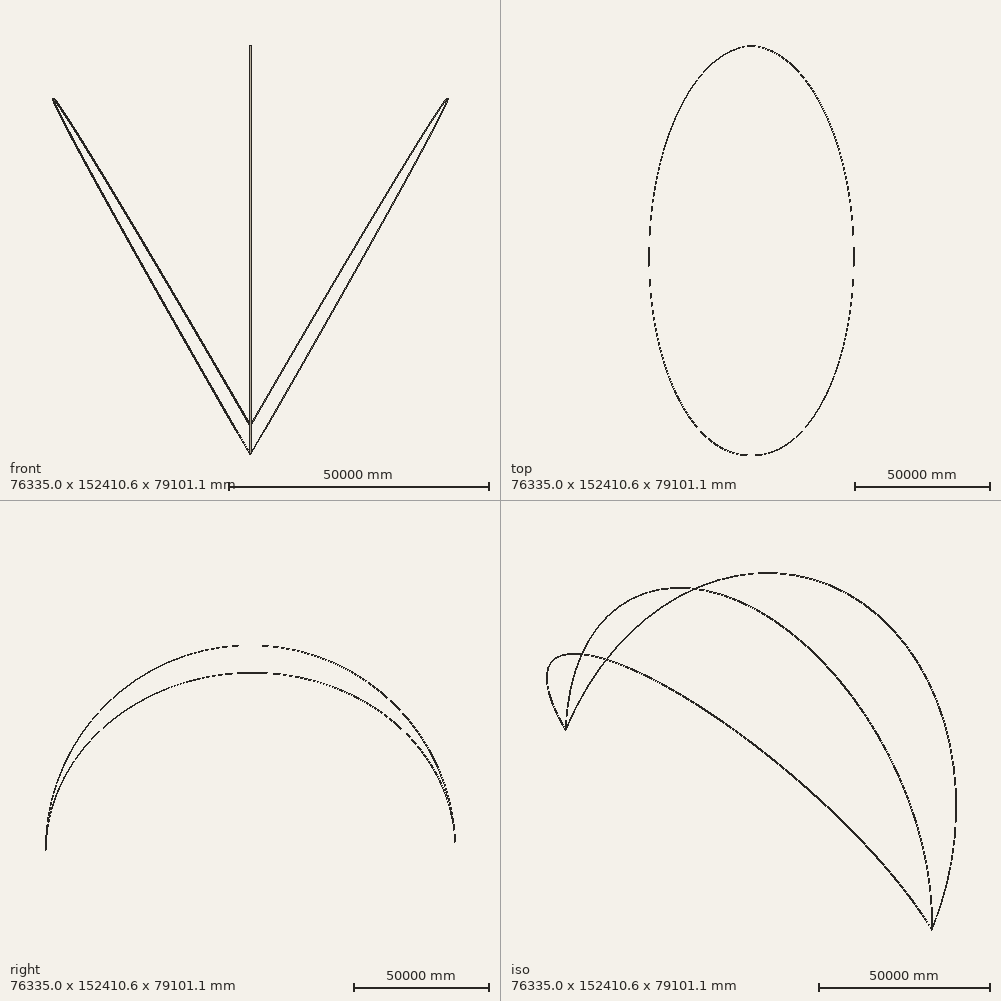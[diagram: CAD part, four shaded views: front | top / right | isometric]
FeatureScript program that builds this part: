
annotation { "Feature Type Name" : "Feature", "Feature Type Description" : "" }
export const myFeature = defineFeature(function(context is Context, id is Id, definition is map)
    precondition{}
    {
        {
            var Q0;
            Q0=qCreatedBy(makeId("Right.planeOp"),FACE);
            var sketch = newSketch(context, id + "F0", { "sketchPlane" : qUnion([Q0])});
            skArc(sketch, "E0", {"start": v(76147.78, 2820.45) * mm, "mid": v(-2820.45, 76147.78) * mm, "end": v(-76147.78, -2820.45) * mm});
            skLineSegment(sketch, "E1", {"start": v(76147.78, 2820.45) * mm, "end": v(-76147.78, -2820.45) * mm});
            skSolve(sketch);
        }
        {
            var Q0;
            Q0=makeQuery(id+"F0.imprint","IMPRINT",FACE,{"disambiguationData":[TD([[makeQuery(id+"F0.imprint","IMPRINT",EDGE,{"derivedFrom":sQuery(id+"F0.wireOp",EDGE,"E0")}),1.0]])]});
            var Q1;
            Q1=sQuery(id+"F0.wireOp",EDGE,"E1");
            cPlane(context, id + "F1", {"entities" : qUnion([Q0, Q1]), "cplaneType" : CPlaneType.LINE_ANGLE, "offset" : 25.4 * mm, "angle" : 30 * degree, "width" : 152.4 * mm, "height" : 152.4 * mm});
        }
        {
            var Q0;
            Q0=qCreatedBy(makeId("Top.planeOp"),FACE);
            var sketch = newSketch(context, id + "F2", { "sketchPlane" : qUnion([Q0])});
            skCircle(sketch, "E2", {"center": v(0, -76127.78) * mm, "radius": 103.6 * mm});
            skSolve(sketch);
        }
        {
            var Q0;
            Q0 = qSketchRegion(id + "F2", true);
            var Q1;
            Q1=sQuery(id+"F0.wireOp",EDGE,"E0");
            sweep(context, id + "F3", {"profiles" : qUnion([Q0]), "path" : qUnion([Q1])});
        }
        {
            var Q0;
            Q0=makeQuery(id+"F3.opSweep","SWEPT_BODY",BODY,{"disambiguationData":[OSD([sQuery(id+"F0.wireOp",EDGE,"E0"),sQuery(id+"F2.wireOp",EDGE,"E2")])]});
            var Q1;
            Q1=sQuery(id+"F0.wireOp",EDGE,"E1");
            transform(context, id + "F4", {"entities" : qUnion([Q0]), "transformType" : TransformType.ROTATION, "transformAxis" : qUnion([Q1]), "angle" : 30 * degree, "makeCopy" : false});
        }
        {
            var Q0;
            Q0=makeQuery(id+"F3.opSweep","SWEPT_BODY",BODY,{"disambiguationData":[OSD([sQuery(id+"F0.wireOp",EDGE,"E0"),sQuery(id+"F2.wireOp",EDGE,"E2")])]});
            var Q1;
            Q1=sQuery(id+"F0.wireOp",EDGE,"E1");
            circularPattern(context, id + "F5", {"operationType" : NewBodyOperationType.ADD, "entities" : qUnion([Q0]), "axis" : qUnion([Q1]), "angle" : 60 * degree, "instanceCount" : 3, "oppositeDirection" : true, "equalSpace" : true});
        }
    });
